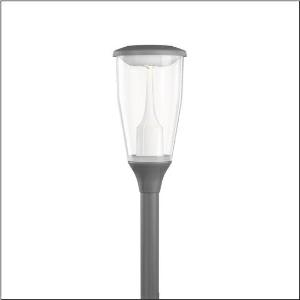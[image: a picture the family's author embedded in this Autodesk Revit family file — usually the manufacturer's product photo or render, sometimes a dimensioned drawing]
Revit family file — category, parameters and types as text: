
# Revit family: dl_11_iq___p1_0a_5xa5575lf14h000022_ea02
name_source: partatom
category: Lighting Fixtures
units: mm (PartAtom-declared; Revit-internal decimal feet)

## family parameters
Cut with Voids When Loaded = No
Host = Face
Light Source = No
Part Type = Normal
Room Calculation Point = No
Round Connector Dimension = Use Diameter
Shared = No

## types (1)
- --- (1 x LED, 1530 lm, 10 W, 4000K)
    Apparent Load = 10 VA
    CIE Flux Codes = 34 63 91 95 100
    Color Rendering = 70
    Color Temperature = 4000K
    Default Elevation = 1800 mm
    Description = DL 11 iQ, mast luminaire, Module 540 iQ-SR, primary light control with 3 zone facetted reflector, of plastic, silver coated, highly specular, structured, primary optical cover: cover, of PMMA, transparent, light distribution: P1.0a, light emission: direct distribution, primary light characteristic: asymmetric, installation type: post-top, LED, High Power LED, light colour: 740, colour temperature: 4000K, control: Street-Remote, Auto-Match, Temp-Guard, Lumen-Switch, Night-Set, Smart-Wire, Light-Fading, Desk-Remote (wireless, voltage-free reading and setting of iQ features in the workshop via application-optimized NFC function/RFID function), optimised constant luminous flux control (CLO 2.0), mains connection: 220..240V, AC, 50/60Hz, connection cable pre-assembled, cable length: 5,5m, start of lifetime: 10W, end of service life: 10W, luminaire housing, upper part, of diecast aluminium, coated, Siteco® metallic grey (DB 702S), spigot size: 76mm (post-top), post-top mast mounting element, of diecast aluminium, coated, Siteco® metallic grey (DB 702S), Module 540 iQ-SR, traffic white (RAL 9016), equipment: standard, protection rating (complete): IP66, insulation class (complete): insulation class II (safety insulation), certification: CE, ENEC, ENEC+, VDE, packaging unit: 1 piece

Light Distribution: P1.0a
    Height = 665 mm
    Lamp = 1 x LED
    Lamp Light Flux = 1530 lm
    Lamp Power = 10 W
    Lamp count = 1
    Length = 334 mm
    Luminous efficacy = 153 lm/W
    Manufacturer = Siteco
    ModVariant = No
    Model = 5XA5575LF14H000022
    Number of Poles = 1
    OnlyDefault = Yes
    Power Factor = 1
    Product Name = DL 11 iQ | P1.0a
    Product group = mast luminaire | pylon top
    ProductGroupID = 6100
    Protection Class = Protection class II
    Protection Degree = IP 66
    RLX_Detail_Level = 1
    RLX_Emergency_Light_Flux = 0 lm
    RLX_Emergency_Type = 0
    RLX_Emergency_Type_DB = No
    RlxData = <blob elided: 107481 chars, md5=eff24301>
    Socket = socket
    Standby Power = 0 W
    System Light Flux = 1530 lm
    System Power = 10 W
    Type Comments = factory setting: luminous flux: 100 % | dim-lin: 254 | 401 mA
    Type Image = l_1258354.jpg
    URL = http://relux.com
    VarID = @adj_042275
    Voltage = 0 V
    Weight = 0.00 kg
    Width = 0 mm  [stored 0 ft]

note: [stored X ft] marks values corroborated as IEEE doubles in the binary element streams (Revit-internal decimal feet)

## geometry (parser evidence)
native form markers: Blend x4, Sweep x10
no freeform markers — native parametric forms only
